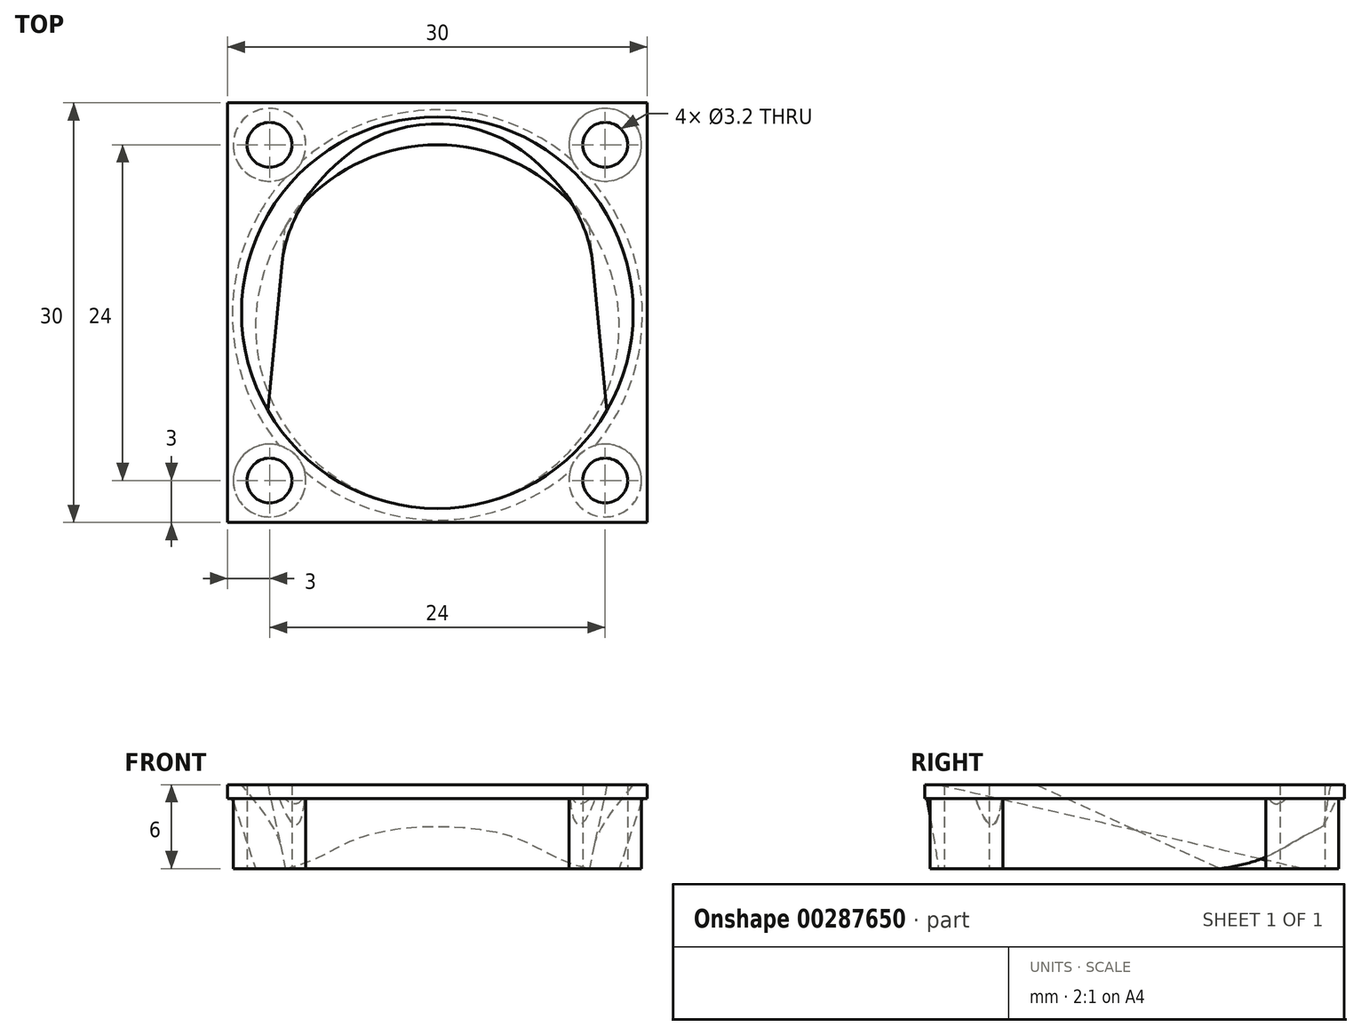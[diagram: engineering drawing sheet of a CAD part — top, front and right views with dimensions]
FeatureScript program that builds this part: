
annotation { "Feature Type Name" : "Feature", "Feature Type Description" : "" }
export const myFeature = defineFeature(function(context is Context, id is Id, definition is map)
    precondition{}
    {
        {
            var Q0;
            Q0=qCreatedBy(makeId("Top.planeOp"),FACE);
            var sketch = newSketch(context, id + "F0", { "sketchPlane" : qUnion([Q0])});
            skLineSegment(sketch, "E0.bottom", {"start": v(15, -15) * mm, "end": v(-15, -15) * mm});
            skLineSegment(sketch, "E0.top", {"start": v(15, 15) * mm, "end": v(-15, 15) * mm});
            skLineSegment(sketch, "E0.left", {"start": v(15, -15) * mm, "end": v(15, 15) * mm});
            skLineSegment(sketch, "E0.right", {"start": v(-15, -15) * mm, "end": v(-15, 15) * mm});
            skPoint(sketch, "E0.middle", {"position": v(0, 0) * mm});
            skLineSegment(sketch, "E1.bottom", {"start": v(12, -12) * mm, "end": v(-12, -12) * mm, "construction": true});
            skLineSegment(sketch, "E1.top", {"start": v(12, 12) * mm, "end": v(-12, 12) * mm, "construction": true});
            skLineSegment(sketch, "E1.left", {"start": v(12, -12) * mm, "end": v(12, 12) * mm, "construction": true});
            skLineSegment(sketch, "E1.right", {"start": v(-12, -12) * mm, "end": v(-12, 12) * mm, "construction": true});
            skCircle(sketch, "E2", {"center": v(-12, 12) * mm, "radius": 1.6 * mm});
            skCircle(sketch, "E3", {"center": v(12, 12) * mm, "radius": 1.6 * mm});
            skCircle(sketch, "E4", {"center": v(-12, -12) * mm, "radius": 1.6 * mm});
            skCircle(sketch, "E5", {"center": v(12, -12) * mm, "radius": 1.6 * mm});
            skSolve(sketch);
        }
        {
            var Q0;
            Q0 = qSketchRegion(id + "F0", true);
            extrude(context, id + "F1", {"entities" : qUnion([Q0]), "depth" : 1 * mm, "offsetDistance" : 25 * mm});
        }
        {
            var Q0;
            Q0=makeQuery(id+"F1.opExtrude","CAP_FACE",FACE,{"disambiguationData":[OSD([sQuery(id+"F0.wireOp",EDGE,"E0.bottom"),sQuery(id+"F0.wireOp",EDGE,"E0.top"),sQuery(id+"F0.wireOp",EDGE,"E0.left"),sQuery(id+"F0.wireOp",EDGE,"E0.right"),sQuery(id+"F0.wireOp",EDGE,"E2"),sQuery(id+"F0.wireOp",EDGE,"E3"),sQuery(id+"F0.wireOp",EDGE,"E4"),sQuery(id+"F0.wireOp",EDGE,"E5")])],"isStart":true});
            var sketch = newSketch(context, id + "F2", { "sketchPlane" : qUnion([Q0])});
            skCircle(sketch, "E6", {"center": v(-12, 12) * mm, "radius": 2.6 * mm});
            skCircle(sketch, "E7.0", {"center": v(-12, 12) * mm, "radius": 1.6 * mm});
            skCircle(sketch, "E8.0", {"center": v(-12, -12) * mm, "radius": 1.6 * mm});
            skCircle(sketch, "E9", {"center": v(-12, -12) * mm, "radius": 2.6 * mm});
            skSolve(sketch);
        }
        {
            var Q0;
            Q0 = qSketchRegion(id + "F2", true);
            extrude(context, id + "F3", {"entities" : qUnion([Q0]), "operationType" : NewBodyOperationType.ADD, "depth" : 5 * mm, "offsetDistance" : 25 * mm});
        }
        {
            var Q0;
            Q0=makeQuery(id+"F1.opExtrude","SWEPT_BODY",BODY,{"disambiguationData":[OSD([sQuery(id+"F0.wireOp",EDGE,"E0.bottom"),sQuery(id+"F0.wireOp",EDGE,"E0.top"),sQuery(id+"F0.wireOp",EDGE,"E0.left"),sQuery(id+"F0.wireOp",EDGE,"E0.right"),sQuery(id+"F0.wireOp",EDGE,"E2"),sQuery(id+"F0.wireOp",EDGE,"E3"),sQuery(id+"F0.wireOp",EDGE,"E4"),sQuery(id+"F0.wireOp",EDGE,"E5")])]});
            var Q1;
            Q1=qCreatedBy(makeId("Right.planeOp"),FACE);
            mirror(context, id + "F4", {"operationType" : NewBodyOperationType.ADD, "entities" : qUnion([Q0]), "mirrorPlane" : qUnion([Q1])});
        }
        {
            var Q0;
            Q0=makeQuery(id+"F3.opExtrude","CAP_FACE",FACE,{"disambiguationData":[OSD([sQuery(id+"F2.wireOp",EDGE,"E8.0"),sQuery(id+"F2.wireOp",EDGE,"E9")])],"isStart":false});
            var sketch = newSketch(context, id + "F5", { "sketchPlane" : qUnion([Q0])});
            skCircle(sketch, "E10", {"center": v(0, 1) * mm, "radius": 13 * mm});
            skSolve(sketch);
        }
        {
            var Q0;
            Q0=makeQuery(id+"F1.opExtrude","CAP_FACE",FACE,{"disambiguationData":[OSD([sQuery(id+"F0.wireOp",EDGE,"E0.bottom"),sQuery(id+"F0.wireOp",EDGE,"E0.top"),sQuery(id+"F0.wireOp",EDGE,"E0.left"),sQuery(id+"F0.wireOp",EDGE,"E0.right"),sQuery(id+"F0.wireOp",EDGE,"E2"),sQuery(id+"F0.wireOp",EDGE,"E3"),sQuery(id+"F0.wireOp",EDGE,"E4"),sQuery(id+"F0.wireOp",EDGE,"E5")])],"isStart":false});
            var sketch = newSketch(context, id + "F6", { "sketchPlane" : qUnion([Q0])});
            skCircle(sketch, "E11", {"center": v(0, 0) * mm, "radius": 15 * mm});
            skSolve(sketch);
        }
        {
            var Q0;
            Q0 = qSketchRegion(id + "F5", true);
            var Q1;
            {var subQ0=sQuery(id+"F6.wireOp",EDGE,"E11");var subQ1=makeQuery(id+"F6.imprint","INTERSECT",VERTEX,{"derivedFrom":[makeQuery(id+"F1.opExtrude","CAP_EDGE",EDGE,{"disambiguationData":[OSD([sQuery(id+"F0.wireOp",EDGE,"E0.top")])],"isStart":false}),subQ0]});Q1=makeQuery(id+"F6.imprint","IMPRINT",FACE,{"disambiguationData":[TD([[makeQuery(id+"F6.imprint","IMPRINT",EDGE,{"disambiguationData":[TD([[subQ1,1.0]])],"derivedFrom":subQ0}),1.0]])]});}
            loft(context, id + "F7", {"operationType" : NewBodyOperationType.ADD, "sheetProfilesArray" : [{ "sheetProfileEntities" : qUnion([Q0]) }, { "sheetProfileEntities" : qUnion([Q1]) }]});
        }
        {
            var Q0;
            Q0=makeQuery(id+"F7.opLoft","CAP_FACE",FACE,{"disambiguationData":[OSD([makeQuery(id+"F5.imprint","IMPRINT",FACE,{"disambiguationData":[TD([[makeQuery(id+"F5.imprint","IMPRINT",EDGE,{"derivedFrom":sQuery(id+"F5.wireOp",EDGE,"E10")}),1.0]])]})])],"isStart":true});
            var sketch = newSketch(context, id + "F8", { "sketchPlane" : qUnion([Q0])});
            skFitSpline(sketch, "E12.0", {"points": [v(0, -13) * mm, v(0.4, -13) * mm, v(1.18, -12.96) * mm, v(2.35, -12.79) * mm, v(3.49, -12.5) * mm, v(4.6, -12.1) * mm, v(5.67, -11.6) * mm, v(6.68, -11) * mm, v(7.62, -10.3) * mm, v(8.5, -9.5) * mm, v(9.3, -8.63) * mm, v(10, -7.68) * mm, v(10.6, -6.67) * mm, v(11.1, -5.6) * mm, v(11.5, -4.49) * mm, v(11.79, -3.34) * mm, v(11.96, -2.18) * mm, v(12, -1.4) * mm, v(12, -1) * mm]});
            skFitSpline(sketch, "E12.1", {"points": [v(-12, -1) * mm, v(-12, -1.4) * mm, v(-11.96, -2.18) * mm, v(-11.79, -3.35) * mm, v(-11.5, -4.49) * mm, v(-11.1, -5.6) * mm, v(-10.6, -6.67) * mm, v(-10, -7.68) * mm, v(-9.3, -8.62) * mm, v(-8.5, -9.5) * mm, v(-7.63, -10.3) * mm, v(-6.68, -11) * mm, v(-5.67, -11.6) * mm, v(-4.6, -12.1) * mm, v(-3.49, -12.5) * mm, v(-2.34, -12.79) * mm, v(-1.18, -12.96) * mm, v(-0.4, -13) * mm, v(0, -13) * mm]});
            skFitSpline(sketch, "E12.2", {"points": [v(0, 11) * mm, v(-0.4, 11) * mm, v(-1.18, 10.96) * mm, v(-2.35, 10.79) * mm, v(-3.49, 10.5) * mm, v(-4.6, 10.1) * mm, v(-5.67, 9.6) * mm, v(-6.68, 9) * mm, v(-7.62, 8.3) * mm, v(-8.5, 7.5) * mm, v(-9.3, 6.63) * mm, v(-10, 5.68) * mm, v(-10.6, 4.67) * mm, v(-11.1, 3.6) * mm, v(-11.5, 2.49) * mm, v(-11.79, 1.34) * mm, v(-11.96, 0.18) * mm, v(-12, -0.6) * mm, v(-12, -1) * mm]});
            skFitSpline(sketch, "E12.3", {"points": [v(12, -1) * mm, v(12, -0.6) * mm, v(11.96, 0.18) * mm, v(11.79, 1.35) * mm, v(11.5, 2.49) * mm, v(11.1, 3.6) * mm, v(10.6, 4.67) * mm, v(10, 5.68) * mm, v(9.3, 6.62) * mm, v(8.5, 7.5) * mm, v(7.63, 8.3) * mm, v(6.68, 9) * mm, v(5.67, 9.6) * mm, v(4.6, 10.1) * mm, v(3.49, 10.5) * mm, v(2.34, 10.79) * mm, v(1.18, 10.96) * mm, v(0.4, 11) * mm, v(0, 11) * mm]});
            skSolve(sketch);
        }
        {
            var Q0;
            Q0=makeQuery(id+"F1.opExtrude","CAP_FACE",FACE,{"disambiguationData":[OSD([sQuery(id+"F0.wireOp",EDGE,"E0.bottom"),sQuery(id+"F0.wireOp",EDGE,"E0.top"),sQuery(id+"F0.wireOp",EDGE,"E0.left"),sQuery(id+"F0.wireOp",EDGE,"E0.right"),sQuery(id+"F0.wireOp",EDGE,"E2"),sQuery(id+"F0.wireOp",EDGE,"E3"),sQuery(id+"F0.wireOp",EDGE,"E4"),sQuery(id+"F0.wireOp",EDGE,"E5")])],"isStart":false});
            var sketch = newSketch(context, id + "F9", { "sketchPlane" : qUnion([Q0])});
            skCircle(sketch, "E13", {"center": v(0, 0) * mm, "radius": 14 * mm});
            skSolve(sketch);
        }
        {
            var Q1;
            Q1=makeQuery(id+"F9.imprint","IMPRINT",FACE,{"disambiguationData":[TD([[makeQuery(id+"F9.imprint","IMPRINT",EDGE,{"derivedFrom":sQuery(id+"F9.wireOp",EDGE,"E13")}),1.0]])]});
            var Q2;
            Q2=makeQuery(id+"F8.imprint","IMPRINT",FACE,{"disambiguationData":[TD([[makeQuery(id+"F8.imprint","IMPRINT",EDGE,{"derivedFrom":sQuery(id+"F8.wireOp",EDGE,"E12.0")}),1.0]])]});
            loft(context, id + "F10", {"operationType" : NewBodyOperationType.REMOVE, "sheetProfilesArray" : [{ "sheetProfileEntities" : qUnion([Q1]) }, { "sheetProfileEntities" : qUnion([Q2]) }]});
        }
    });
